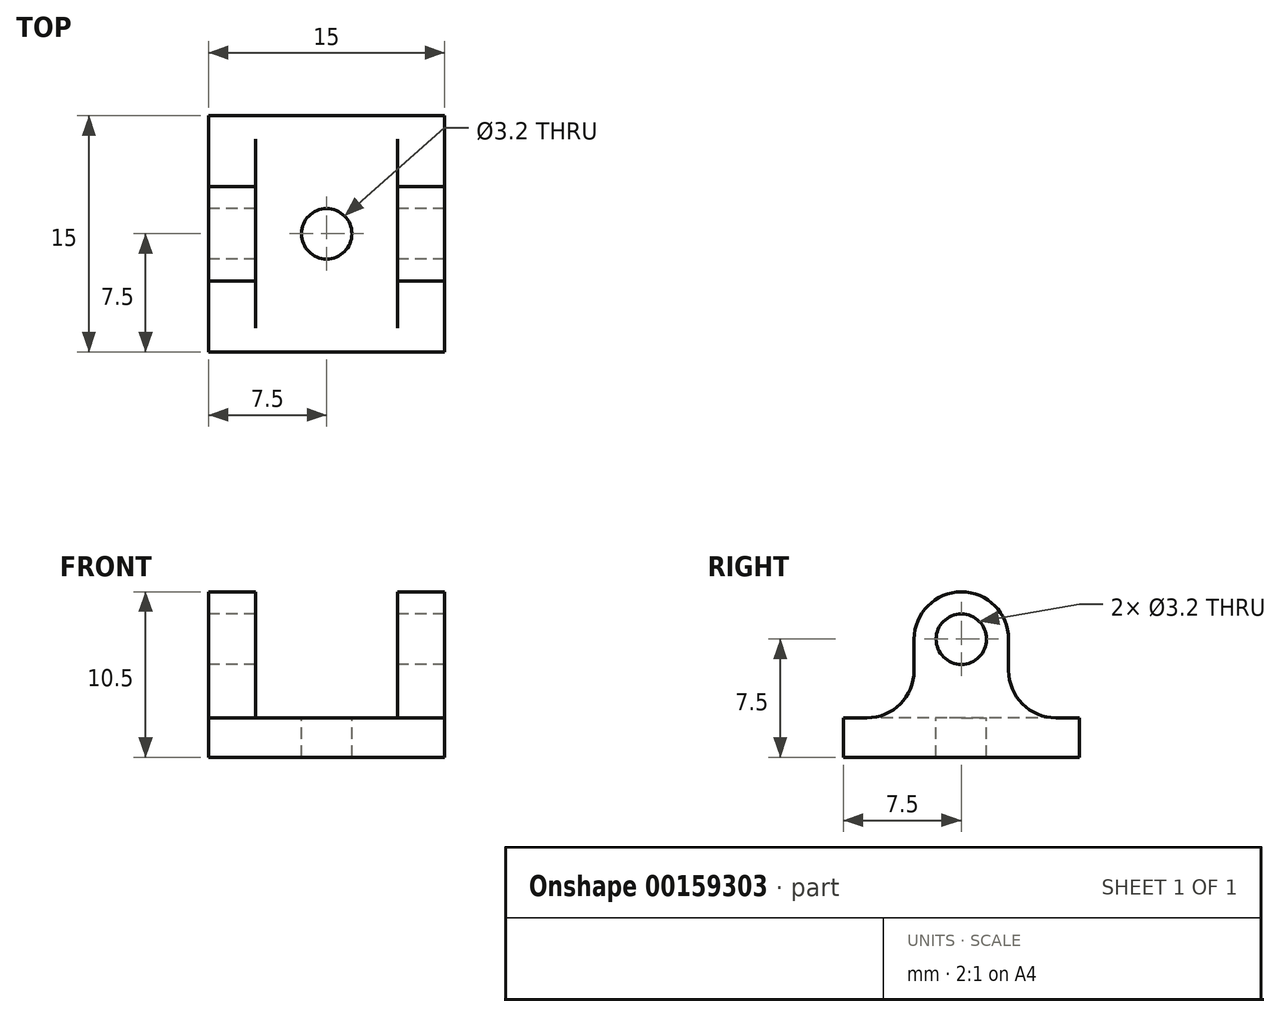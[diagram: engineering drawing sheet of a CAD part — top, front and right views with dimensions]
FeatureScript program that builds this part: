
annotation { "Feature Type Name" : "Feature", "Feature Type Description" : "" }
export const myFeature = defineFeature(function(context is Context, id is Id, definition is map)
    precondition{}
    {
        {
            var Q0;
            Q0=qCreatedBy(makeId("Right.planeOp"),FACE);
            var sketch = newSketch(context, id + "F0", { "sketchPlane" : qUnion([Q0])});
            skCircle(sketch, "E0", {"center": v(0, 0) * mm, "radius": 1.6 * mm});
            skArc(sketch, "E1", {"start": v(-3, 0) * mm, "mid": v(0, 3) * mm, "end": v(3, 0) * mm});
            skLineSegment(sketch, "E2", {"start": v(-3, 0) * mm, "end": v(-3, -5) * mm});
            skLineSegment(sketch, "E3", {"start": v(-3, -5) * mm, "end": v(-7.5, -5) * mm});
            skLineSegment(sketch, "E4", {"start": v(-7.5, -5) * mm, "end": v(-7.5, -7.5) * mm});
            skLineSegment(sketch, "E5", {"start": v(-7.5, -7.5) * mm, "end": v(7.5, -7.5) * mm});
            skLineSegment(sketch, "E6", {"start": v(7.5, -7.5) * mm, "end": v(7.5, -5) * mm});
            skLineSegment(sketch, "E7", {"start": v(7.5, -5) * mm, "end": v(3, -5) * mm});
            skLineSegment(sketch, "E8", {"start": v(3, -5) * mm, "end": v(3, 0) * mm});
            skSolve(sketch);
        }
        {
            var Q0;
            Q0=makeQuery(id+"F0.imprint","IMPRINT",FACE,{"disambiguationData":[TD([[makeQuery(id+"F0.imprint","IMPRINT",EDGE,{"derivedFrom":sQuery(id+"F0.wireOp",EDGE,"E0")}),-1.0]])]});
            extrude(context, id + "F1", {"entities" : qUnion([Q0]), "endBound" : BoundingType.SYMMETRIC, "depth" : (9 + 3 + 3) * mm});
        }
        {
            var Q0;
            Q0=makeQuery(id+"F1.opExtrude","SWEPT_EDGE",EDGE,{"disambiguationData":[OSD([sQuery(id+"F0.wireOp",EDGE,"E2"),sQuery(id+"F0.wireOp",EDGE,"E3")])]});
            var Q1;
            Q1=makeQuery(id+"F1.opExtrude","SWEPT_EDGE",EDGE,{"disambiguationData":[OSD([sQuery(id+"F0.wireOp",EDGE,"E7"),sQuery(id+"F0.wireOp",EDGE,"E8")])]});
            fillet(context, id + "F2", {"entities" : qUnion([Q0, Q1]), "radius" : 3 * mm, "allowEdgeOverflow" : false});
        }
        {
            var Q0;
            Q0=makeQuery(id+"F1.opExtrude","SWEPT_FACE",FACE,{"disambiguationData":[OSD([sQuery(id+"F0.wireOp",EDGE,"E3")])]});
            var sketch = newSketch(context, id + "F3", { "sketchPlane" : qUnion([Q0])});
            skLineSegment(sketch, "E9.bottom", {"start": v(4.5, 23.22) * mm, "end": v(-4.5, 23.22) * mm});
            skLineSegment(sketch, "E9.top", {"start": v(4.5, -23.22) * mm, "end": v(-4.5, -23.22) * mm});
            skLineSegment(sketch, "E9.left", {"start": v(4.5, 23.22) * mm, "end": v(4.5, -23.22) * mm});
            skLineSegment(sketch, "E9.right", {"start": v(-4.5, 23.22) * mm, "end": v(-4.5, -23.22) * mm});
            skPoint(sketch, "E9.middle", {"position": v(0, 0) * mm});
            skSolve(sketch);
        }
        {
            var Q0;
            Q0 = qSketchRegion(id + "F3", true);
            extrude(context, id + "F4", {"entities" : qUnion([Q0]), "operationType" : NewBodyOperationType.REMOVE, "endBound" : BoundingType.THROUGH_ALL, "depth" : 25 * mm});
        }
        {
            var Q0;
            Q0=qCreatedBy(makeId("Top.planeOp"),FACE);
            var sketch = newSketch(context, id + "F5", { "sketchPlane" : qUnion([Q0])});
            skPoint(sketch, "E10", {"position": v(0, 0) * mm});
            skSolve(sketch);
        }
        {
            var Q0;
            Q0=sQuery(id+"F5.wireOp",VERTEX,"E10");
            var Q1;
            Q1=makeQuery(id+"F1.opExtrude","SWEPT_BODY",BODY,{"disambiguationData":[OSD([sQuery(id+"F0.wireOp",EDGE,"E0"),sQuery(id+"F0.wireOp",EDGE,"E1"),sQuery(id+"F0.wireOp",EDGE,"E2"),sQuery(id+"F0.wireOp",EDGE,"E3"),sQuery(id+"F0.wireOp",EDGE,"E4"),sQuery(id+"F0.wireOp",EDGE,"E5"),sQuery(id+"F0.wireOp",EDGE,"E6"),sQuery(id+"F0.wireOp",EDGE,"E7"),sQuery(id+"F0.wireOp",EDGE,"E8")])]});
            hole(context, id + "F6", {"style" : HoleStyle.SIMPLE, "endStyle" : HoleEndStyle.THROUGH, "holeDiameter" : 3.2 * mm, "locations" : qUnion([Q0]), "scope" : qUnion([Q1]), "isTappedThrough" : true});
        }
    });
